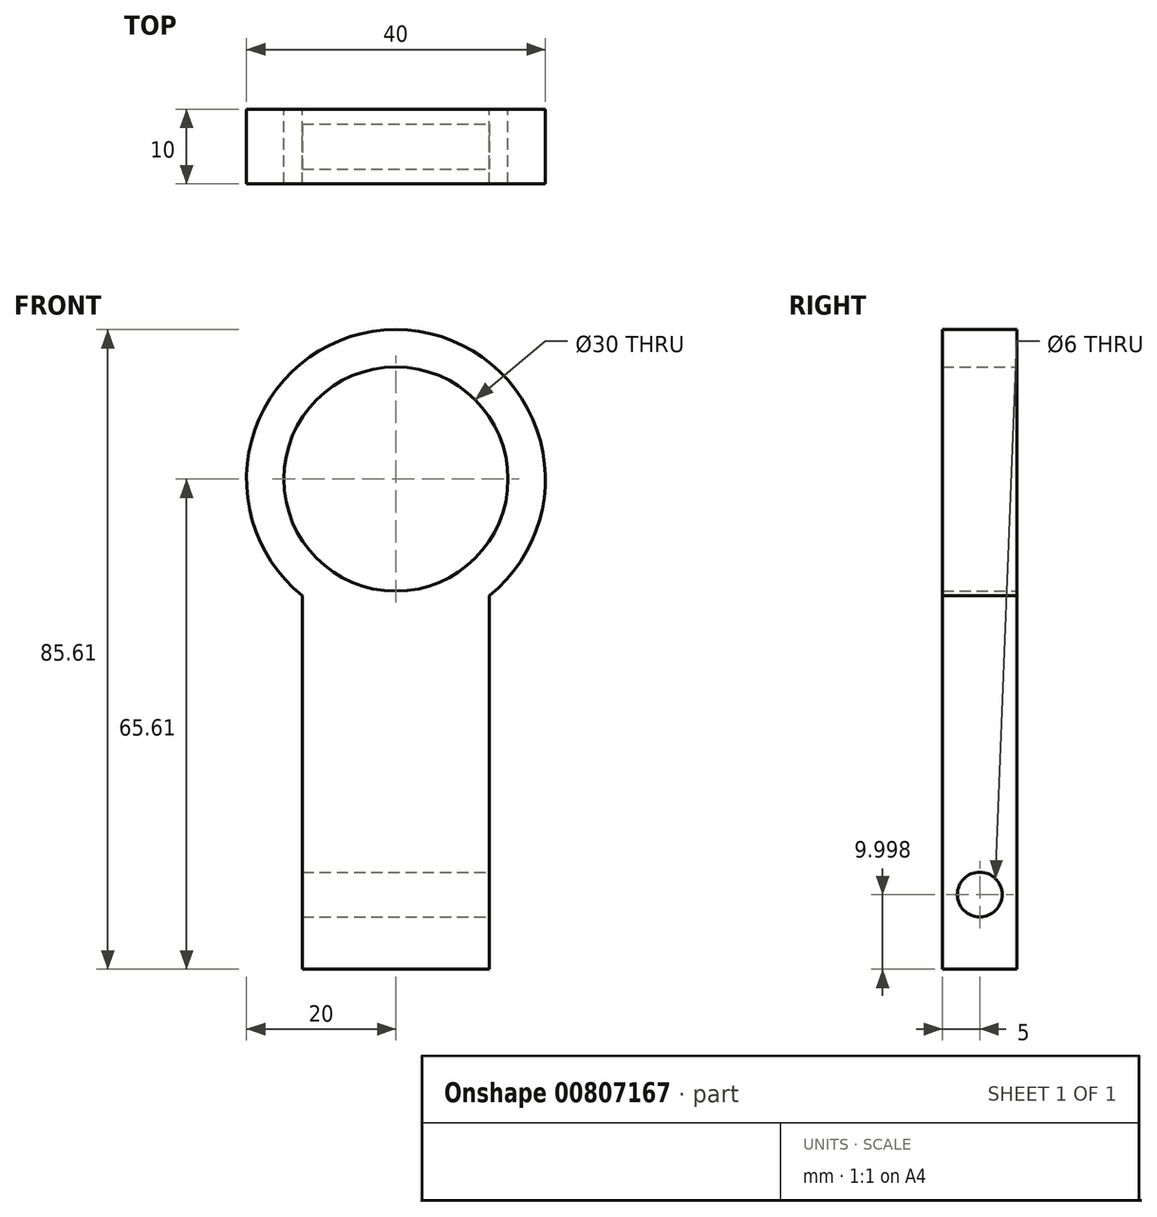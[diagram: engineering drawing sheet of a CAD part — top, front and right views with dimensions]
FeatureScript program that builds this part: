
annotation { "Feature Type Name" : "Feature", "Feature Type Description" : "" }
export const myFeature = defineFeature(function(context is Context, id is Id, definition is map)
    precondition{}
    {
        {
            var Q0;
            Q0=qCreatedBy(makeId("Front.planeOp"),FACE);
            var sketch = newSketch(context, id + "F0", { "sketchPlane" : qUnion([Q0])});
            skCircle(sketch, "E0", {"center": v(0, 0) * mm, "radius": 15 * mm});
            skCircle(sketch, "E1", {"center": v(0, 0) * mm, "radius": 20 * mm});
            skLineSegment(sketch, "E2.bottom", {"start": v(12.5, -15.61) * mm, "end": v(-12.5, -15.61) * mm});
            skLineSegment(sketch, "E2.top", {"start": v(12.5, -65.61) * mm, "end": v(-12.5, -65.61) * mm});
            skLineSegment(sketch, "E2.left", {"start": v(12.5, -15.61) * mm, "end": v(12.5, -65.61) * mm});
            skLineSegment(sketch, "E2.right", {"start": v(-12.5, -15.61) * mm, "end": v(-12.5, -65.61) * mm});
            skSolve(sketch);
        }
        {
            var Q0;
            Q0=makeQuery(id+"F0.imprint","IMPRINT",FACE,{"disambiguationData":[TD([[makeQuery(id+"F0.imprint","IMPRINT",EDGE,{"derivedFrom":sQuery(id+"F0.wireOp",EDGE,"E0")}),-1.0]])]});
            var Q1;
            Q1=makeQuery(id+"F0.imprint","IMPRINT",FACE,{"disambiguationData":[TD([[makeQuery(id+"F0.imprint","IMPRINT",EDGE,{"derivedFrom":sQuery(id+"F0.wireOp",EDGE,"E2.top")}),-1.0]])]});
            var Q2;
            {var subQ0=sQuery(id+"F0.wireOp",EDGE,"E2.bottom");Q2=makeQuery(id+"F0.imprint","IMPRINT",FACE,{"disambiguationData":[TD([[makeQuery(id+"F0.imprint","IMPRINT",EDGE,{"derivedFrom":subQ0}),1.0]])]});}
            extrude(context, id + "F1", {"entities" : qUnion([Q0, Q1, Q2]), "depth" : 10 * mm, "offsetDistance" : 25 * mm});
        }
        {
            var Q0;
            Q0=makeQuery(id+"F1.opExtrude","SWEPT_FACE",FACE,{"disambiguationData":[OSD([sQuery(id+"F0.wireOp",EDGE,"E2.left")])]});
            var sketch = newSketch(context, id + "F2", { "sketchPlane" : qUnion([Q0])});
            skPoint(sketch, "E3", {"position": v(-5, -55.61) * mm});
            skPoint(sketch, "E3.positionSnap0", {"position": v(-5, -65.61) * mm});
            skSolve(sketch);
        }
        {
            var Q0;
            Q0=sQuery(id+"F2.wireOp",VERTEX,"E3");
            var Q1;
            Q1=makeQuery(id+"F1.opExtrude","SWEPT_BODY",BODY,{"disambiguationData":[OSD([sQuery(id+"F0.wireOp",EDGE,"E0"),sQuery(id+"F0.wireOp",EDGE,"E1"),sQuery(id+"F0.wireOp",EDGE,"E2.top"),sQuery(id+"F0.wireOp",EDGE,"E2.left"),sQuery(id+"F0.wireOp",EDGE,"E2.right")])]});
            hole(context, id + "F3", {"style" : HoleStyle.SIMPLE, "endStyle" : HoleEndStyle.THROUGH, "holeDiameter" : 6 * mm, "majorDiameter" : 5 * mm, "isTappedThrough" : true, "tappedDepth" : 12 * mm, "tapClearance" : 3, "locations" : qUnion([Q0]), "scope" : qUnion([Q1])});
        }
    });
